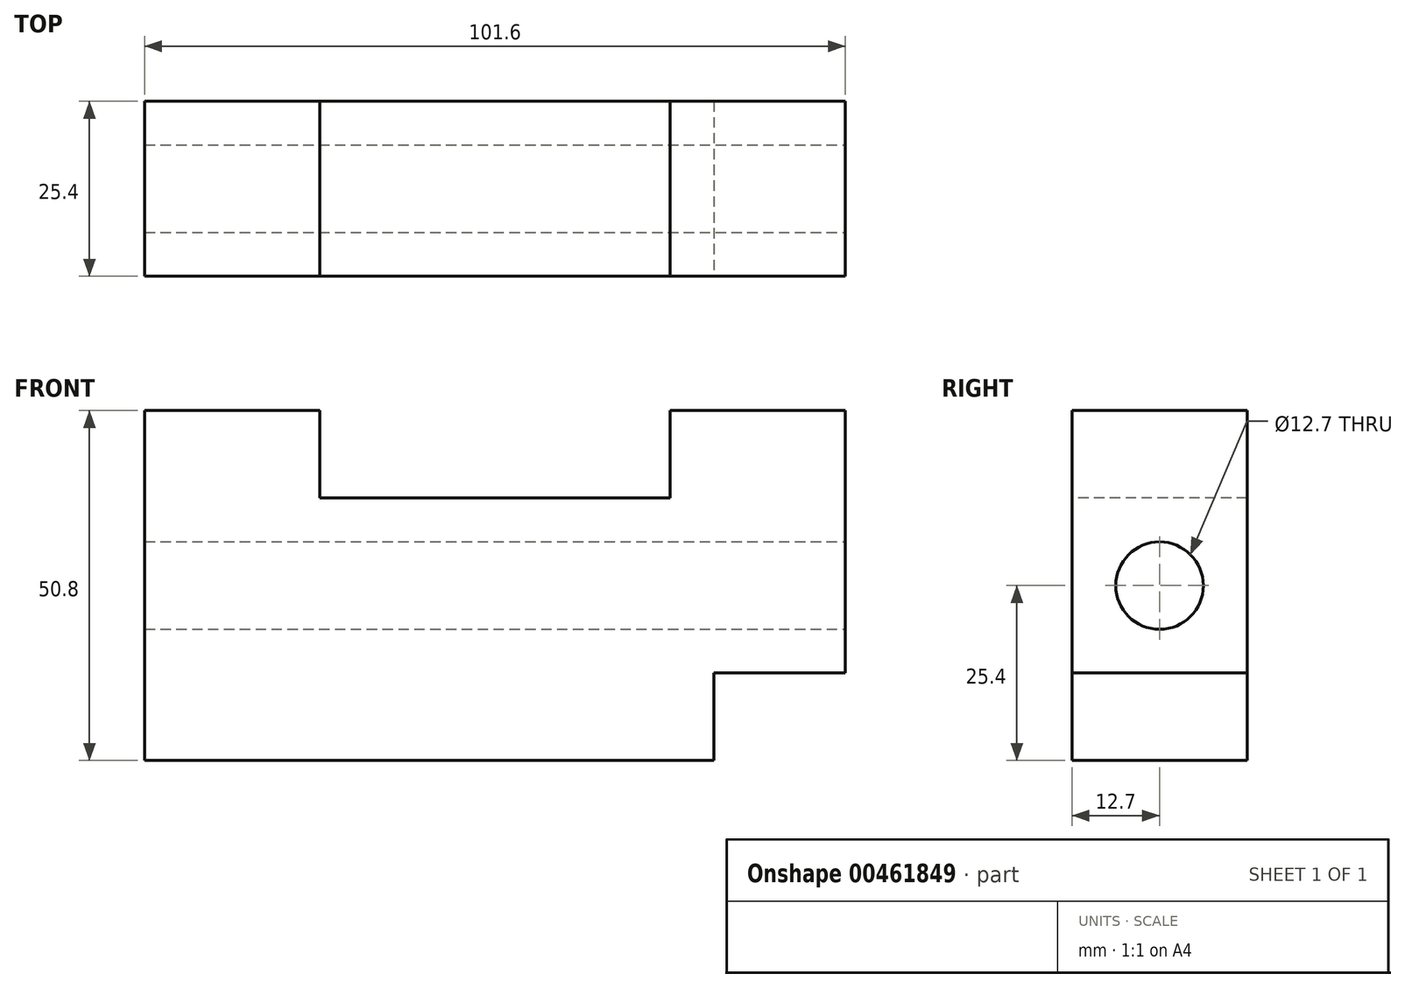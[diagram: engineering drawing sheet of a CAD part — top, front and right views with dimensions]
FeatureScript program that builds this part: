
annotation { "Feature Type Name" : "Feature", "Feature Type Description" : "" }
export const myFeature = defineFeature(function(context is Context, id is Id, definition is map)
    precondition{}
    {
        {
            var Q0;
            Q0=qCreatedBy(makeId("Front.planeOp"),FACE);
            var sketch = newSketch(context, id + "F0", { "sketchPlane" : qUnion([Q0])});
            skLineSegment(sketch, "E0.bottom", {"start": v(50.8, 25.4) * mm, "end": v(-50.8, 25.4) * mm});
            skLineSegment(sketch, "E0.top", {"start": v(50.8, -25.4) * mm, "end": v(-50.8, -25.4) * mm});
            skLineSegment(sketch, "E0.left", {"start": v(50.8, 25.4) * mm, "end": v(50.8, -25.4) * mm});
            skLineSegment(sketch, "E0.right", {"start": v(-50.8, 25.4) * mm, "end": v(-50.8, -25.4) * mm});
            skPoint(sketch, "E0.middle", {"position": v(0, 0) * mm});
            skSolve(sketch);
        }
        {
            var Q0;
            Q0=makeQuery(id+"F0.imprint","IMPRINT",FACE,{"disambiguationData":[TD([[makeQuery(id+"F0.imprint","IMPRINT",EDGE,{"derivedFrom":sQuery(id+"F0.wireOp",EDGE,"E0.bottom")}),1.0]])]});
            extrude(context, id + "F1", {"entities" : qUnion([Q0]), "depth" : 25.4 * mm});
        }
        {
            var Q0;
            Q0=makeQuery(id+"F1.opExtrude","CAP_FACE",FACE,{"disambiguationData":[OSD([sQuery(id+"F0.wireOp",EDGE,"E0.bottom"),sQuery(id+"F0.wireOp",EDGE,"E0.top"),sQuery(id+"F0.wireOp",EDGE,"E0.left"),sQuery(id+"F0.wireOp",EDGE,"E0.right")])],"isStart":false});
            var sketch = newSketch(context, id + "F2", { "sketchPlane" : qUnion([Q0])});
            skLineSegment(sketch, "E1.bottom", {"start": v(-25.4, 25.4) * mm, "end": v(25.4, 25.4) * mm});
            skLineSegment(sketch, "E1.top", {"start": v(-25.4, 12.7) * mm, "end": v(25.4, 12.7) * mm});
            skLineSegment(sketch, "E1.left", {"start": v(-25.4, 25.4) * mm, "end": v(-25.4, 12.7) * mm});
            skLineSegment(sketch, "E1.right", {"start": v(25.4, 25.4) * mm, "end": v(25.4, 12.7) * mm});
            skSolve(sketch);
        }
        {
            var Q0;
            Q0=makeQuery(id+"F2.imprint","IMPRINT",FACE,{"disambiguationData":[TD([[makeQuery(id+"F2.imprint","IMPRINT",EDGE,{"derivedFrom":sQuery(id+"F2.wireOp",EDGE,"E1.bottom")}),1.0]])]});
            extrude(context, id + "F3", {"entities" : qUnion([Q0]), "operationType" : NewBodyOperationType.REMOVE, "oppositeDirection" : true, "depth" : 25.4 * mm});
        }
        {
            var Q0;
            Q0=makeQuery(id+"F1.opExtrude","CAP_FACE",FACE,{"disambiguationData":[OSD([sQuery(id+"F0.wireOp",EDGE,"E0.bottom"),sQuery(id+"F0.wireOp",EDGE,"E0.top"),sQuery(id+"F0.wireOp",EDGE,"E0.left"),sQuery(id+"F0.wireOp",EDGE,"E0.right")])],"isStart":false});
            var sketch = newSketch(context, id + "F4", { "sketchPlane" : qUnion([Q0])});
            skLineSegment(sketch, "E2.bottom", {"start": v(50.8, -12.7) * mm, "end": v(31.75, -12.7) * mm});
            skLineSegment(sketch, "E2.top", {"start": v(50.8, -25.4) * mm, "end": v(31.75, -25.4) * mm});
            skLineSegment(sketch, "E2.left", {"start": v(50.8, -12.7) * mm, "end": v(50.8, -25.4) * mm});
            skLineSegment(sketch, "E2.right", {"start": v(31.75, -12.7) * mm, "end": v(31.75, -25.4) * mm});
            skSolve(sketch);
        }
        {
            var Q0;
            Q0=makeQuery(id+"F4.imprint","IMPRINT",FACE,{"disambiguationData":[TD([[makeQuery(id+"F4.imprint","IMPRINT",EDGE,{"derivedFrom":sQuery(id+"F4.wireOp",EDGE,"E2.bottom")}),1.0]])]});
            extrude(context, id + "F5", {"entities" : qUnion([Q0]), "operationType" : NewBodyOperationType.REMOVE, "oppositeDirection" : true, "depth" : 25.4 * mm});
        }
        {
            var Q0;
            Q0=makeQuery(id+"F1.opExtrude","SWEPT_FACE",FACE,{"disambiguationData":[OSD([sQuery(id+"F0.wireOp",EDGE,"E0.left")])]});
            var sketch = newSketch(context, id + "F6", { "sketchPlane" : qUnion([Q0])});
            skCircle(sketch, "E3", {"center": v(-12.7, 0) * mm, "radius": 6.35 * mm});
            skSolve(sketch);
        }
        {
            var Q0;
            Q0=makeQuery(id+"F6.imprint","IMPRINT",FACE,{"disambiguationData":[TD([[makeQuery(id+"F6.imprint","IMPRINT",EDGE,{"derivedFrom":sQuery(id+"F6.wireOp",EDGE,"E3")}),1.0]])]});
            extrude(context, id + "F7", {"entities" : qUnion([Q0]), "operationType" : NewBodyOperationType.REMOVE, "oppositeDirection" : true, "depth" : 101.6 * mm});
        }
    });
